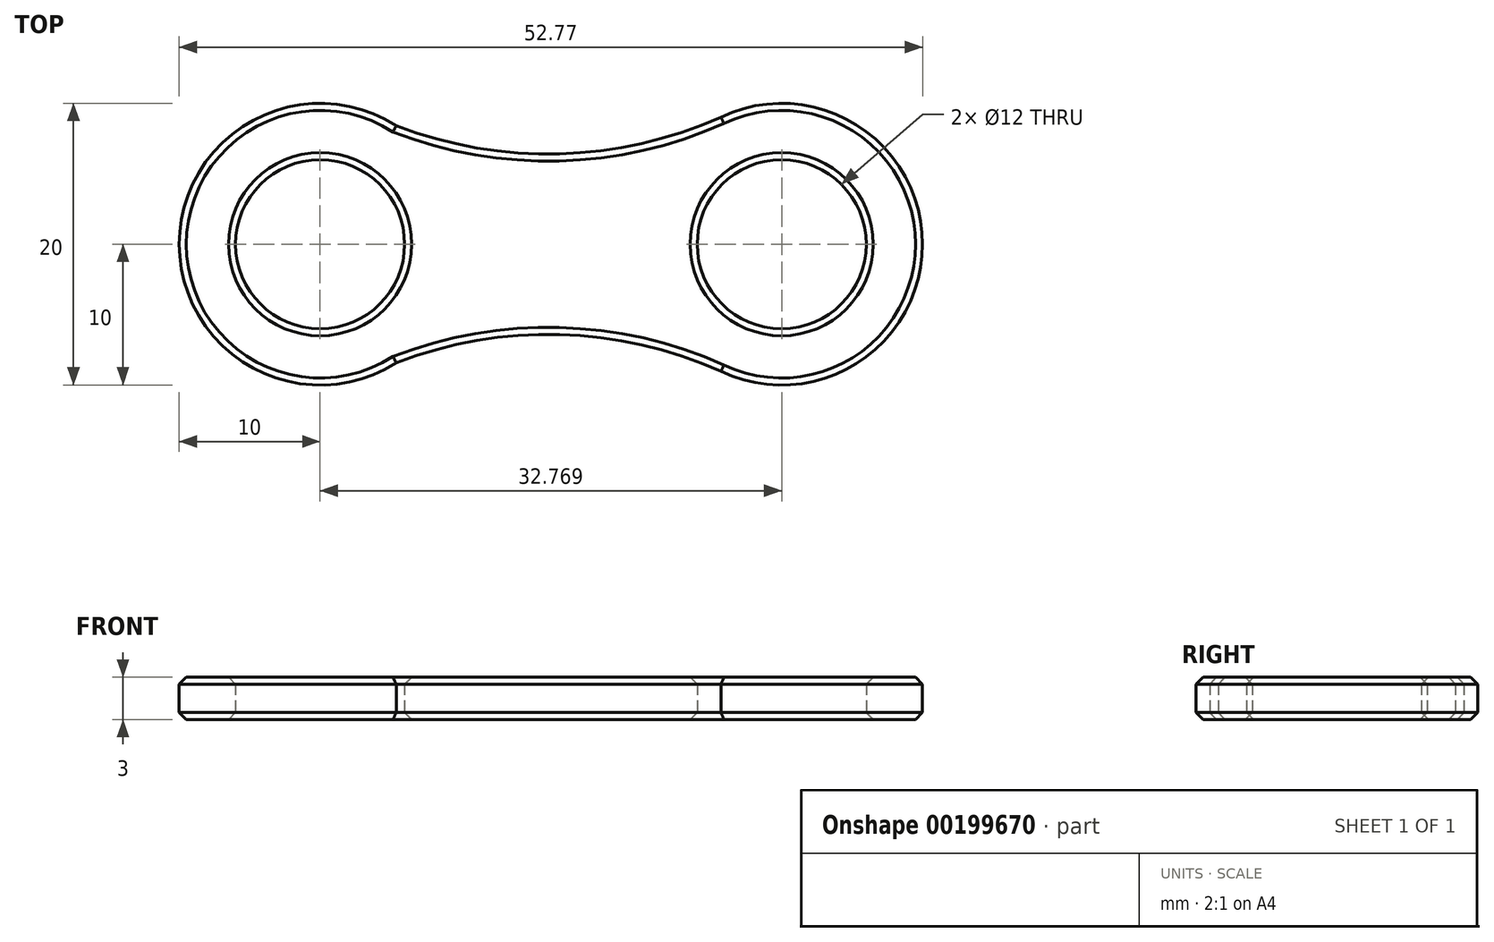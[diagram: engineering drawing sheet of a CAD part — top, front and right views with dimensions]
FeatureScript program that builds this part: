
annotation { "Feature Type Name" : "Feature", "Feature Type Description" : "" }
export const myFeature = defineFeature(function(context is Context, id is Id, definition is map)
    precondition{}
    {
        {
            var Q0;
            Q0=qCreatedBy(makeId("Top.planeOp"),FACE);
            var sketch = newSketch(context, id + "F0", { "sketchPlane" : qUnion([Q0])});
            skArc(sketch, "E0", {"start": v(28.46, -9.02) * mm, "mid": v(42.77, 0) * mm, "end": v(28.46, 9.02) * mm});
            skArc(sketch, "E1", {"start": v(5.4, 8.42) * mm, "mid": v(-10, 0) * mm, "end": v(5.4, -8.42) * mm});
            skArc(sketch, "E2", {"start": v(28.46, -9.02) * mm, "mid": v(17, -6.42) * mm, "end": v(5.4, -8.42) * mm});
            skArc(sketch, "E3", {"start": v(5.4, 8.42) * mm, "mid": v(17, 6.42) * mm, "end": v(28.46, 9.02) * mm});
            skCircle(sketch, "E4", {"center": v(0, 0) * mm, "radius": 6 * mm});
            skCircle(sketch, "E5", {"center": v(32.77, 0) * mm, "radius": 6 * mm});
            skSolve(sketch);
        }
        {
            var Q0;
            Q0=qSketchRegion(id+"F0",true);
            extrude(context, id + "F1", {"entities" : qUnion([Q0]), "depth" : 3 * mm});
        }
        {
            var Q0;
            Q0=makeQuery(id+"F1.opExtrude","CAP_EDGE",EDGE,{"disambiguationData":[OSD([sQuery(id+"F0.wireOp",EDGE,"E2")])],"isStart":false});
            var Q1;
            Q1=makeQuery(id+"F1.opExtrude","CAP_EDGE",EDGE,{"disambiguationData":[OSD([sQuery(id+"F0.wireOp",EDGE,"E0")])],"isStart":false});
            var Q2;
            Q2=makeQuery(id+"F1.opExtrude","CAP_EDGE",EDGE,{"disambiguationData":[OSD([sQuery(id+"F0.wireOp",EDGE,"E1")])],"isStart":true});
            var Q3;
            Q3=makeQuery(id+"F1.opExtrude","CAP_EDGE",EDGE,{"disambiguationData":[OSD([sQuery(id+"F0.wireOp",EDGE,"E1")])],"isStart":false});
            var Q4;
            Q4=makeQuery(id+"F1.opExtrude","CAP_EDGE",EDGE,{"disambiguationData":[OSD([sQuery(id+"F0.wireOp",EDGE,"E3")])],"isStart":false});
            var Q5;
            Q5=makeQuery(id+"F1.opExtrude","CAP_EDGE",EDGE,{"disambiguationData":[OSD([sQuery(id+"F0.wireOp",EDGE,"E2")])],"isStart":true});
            var Q6;
            Q6=makeQuery(id+"F1.opExtrude","CAP_EDGE",EDGE,{"disambiguationData":[OSD([sQuery(id+"F0.wireOp",EDGE,"E3")])],"isStart":true});
            var Q7;
            Q7=makeQuery(id+"F1.opExtrude","CAP_EDGE",EDGE,{"disambiguationData":[OSD([sQuery(id+"F0.wireOp",EDGE,"E0")])],"isStart":true});
            chamfer(context, id + "F2", {"entities" : qUnion([Q0, Q1, Q2, Q3, Q4, Q5, Q6, Q7]), "width" : .5 * mm, "tangentPropagation" : true});
        }
        {
            var Q0;
            Q0=makeQuery(id+"F1.opExtrude","CAP_EDGE",EDGE,{"disambiguationData":[OSD([sQuery(id+"F0.wireOp",EDGE,"E5")])],"isStart":false});
            var Q1;
            Q1=makeQuery(id+"F1.opExtrude","CAP_EDGE",EDGE,{"disambiguationData":[OSD([sQuery(id+"F0.wireOp",EDGE,"E5")])],"isStart":true});
            var Q2;
            Q2=makeQuery(id+"F1.opExtrude","CAP_EDGE",EDGE,{"disambiguationData":[OSD([sQuery(id+"F0.wireOp",EDGE,"E4")])],"isStart":false});
            var Q3;
            Q3=makeQuery(id+"F1.opExtrude","CAP_EDGE",EDGE,{"disambiguationData":[OSD([sQuery(id+"F0.wireOp",EDGE,"E4")])],"isStart":true});
            chamfer(context, id + "F3", {"entities" : qUnion([Q0, Q1, Q2, Q3]), "width" : .5 * mm, "tangentPropagation" : true});
        }
    });
